# Revit family: Mini_System-Carnes-Energy_Recovery-WMA-WMWA-ARR1
name_source: partatom
category: Mechanical Equipment
revit_build: Autodesk Revit Architecture 2012 (Build: 20110309_2315(x64)
units: mm (PartAtom-declared; Revit-internal decimal feet)

## types (12) — shared parameters
Description = Energy Recovery Mini System
Duct Arrangement = 1
Eliminator = Metal - Carnes - Aluminum Frame - Painted White - Mesh
Exhaust Hood Height = 17"
Exhaust Hood Width = 12 1/4"
Exhaust Location From End = 4"
Exhuast Hood Depth = 14 1/4"
Handle = Plastic - Carnes - Smooth - Black
Intake Location From Side = 4"
Manufacturer = CARNES COMPANY
Model = WM_A-ARR1
Product Page URL = http://www.carnes.com
Return Location From Side = 4"
Supply Location From Side = 4"
URL = http://www.carnes.com
Unit = Metal - Carnes - Aluminum Frame - Painted White
Weight = 0.00 lb

## per-type parameters (varying)
| type | Exhaust Height | Exhaust Location From Bottom | Exhaust Width | Height of Unit | Intake Height | Intake Hood Depth | Intake Hood Height | Intake Hood Width | Intake Location From Bottom | Intake Width | Length of Unit | Return Height | Return Location From Bottom | Return Width | Service Clearance Exhaust Side | Service Clearance Supply Side | Size | Supply Height | Supply Location From Bottom | Supply Width | Width of Unit |
| Size 3, Standard | 14" | 6 1/2" | 16" | 47 1/2" | 21" | 18 1/2" | 37" | 19 1/4" | 19" | 16" | 60" | 16" | 6 1/2" | 14" | 50" | 50" | 3 | 14" | 6 1/2" | 16" | 44" |
| Size 3, Water Coils | 14" | 6 1/2" | 16" | 47 1/2" | 21" | 18 1/2" | 37" | 19 1/4" | 19" | 16" | 108" | 16" | 6 1/2" | 14" | 50" | 50" | 3 | 14" | 6 1/2" | 16" | 44" |
| Size 3, Rain Hood | 14" | 6 1/2" | 16" | 47 1/2" | 21" | 18 1/2" | 37" | 19 1/4" | 11" | 16" | 60" | 16" | 6 1/2" | 14" | 50" | 50" | 3 | 14" | 6 1/2" | 16" | 44" |
| Size 3, Rain Hood w/ Water Coils | 14" | 6 1/2" | 16" | 47 1/2" | 21" | 18 1/2" | 37" | 19 1/4" | 11" | 16" | 108" | 16" | 6 1/2" | 14" | 50" | 50" | 3 | 14" | 6 1/2" | 16" | 44" |
| Size 6, Standard | 18" | 6 1/2" | 20" | 57 1/2" | 26" | 26 1/4" | 52 1/2" | 24 1/4" | 24" | 22" | 72" | 20" | 6 1/2" | 18" | 60" | 60" | 6 | 18" | 6 1/2" | 20" | 54" |
| Size 6, Water Coils | 18" | 6 1/2" | 20" | 57 1/2" | 26" | 26 1/4" | 52 1/2" | 24 1/4" | 24" | 22" | 120" | 20" | 6 1/2" | 18" | 60" | 60" | 6 | 18" | 6 1/2" | 20" | 54" |
| Size 6, Rain Hood | 18" | 6 1/2" | 20" | 57 1/2" | 26" | 26 1/4" | 52 1/2" | 24 1/4" | 11" | 22" | 72" | 20" | 6 1/2" | 18" | 60" | 60" | 6 | 18" | 6 1/2" | 20" | 54" |
| Size 6, Rain Hood w/ Water Coils | 18" | 6 1/2" | 20" | 57 1/2" | 26" | 26 1/4" | 52 1/2" | 24 1/4" | 11" | 22" | 120" | 20" | 6 1/2" | 18" | 60" | 60" | 6 | 18" | 6 1/2" | 20" | 54" |
| Size 9, Standard | 20" | 7 1/2" | 24" | 69 1/2" | 34" | 27 1/4" | 55 3/4" | 30 1/2" | 28" | 28" | 80" | 24" | 7 1/2" | 20" | 71" | 71" | 9 | 20" | 7 1/2" | 24" | 66" |
| Size 9, Water Coils | 20" | 7 1/2" | 24" | 69 1/2" | 34" | 27 1/4" | 55 3/4" | 30 1/2" | 28" | 28" | 128" | 24" | 7 1/2" | 20" | 71" | 71" | 9 | 20" | 7 1/2" | 24" | 66" |
| Size 9, Rain Hood | 20" | 7 1/2" | 24" | 69 1/2" | 34" | 27 1/4" | 55 3/4" | 30 1/2" | 17" | 28" | 80" | 24" | 7 1/2" | 20" | 71" | 71" | 9 | 20" | 7 1/2" | 24" | 66" |
| Size 9, Rain Hood w/ Water Coils | 20" | 7 1/2" | 24" | 69 1/2" | 34" | 27 1/4" | 55 3/4" | 30 1/2" | 17" | 28" | 128" | 24" | 7 1/2" | 20" | 71" | 71" | 9 | 20" | 7 1/2" | 24" | 66" |

## geometry (parser evidence)
native form markers: Blend x6, Sweep x9
no freeform markers — native parametric forms only
